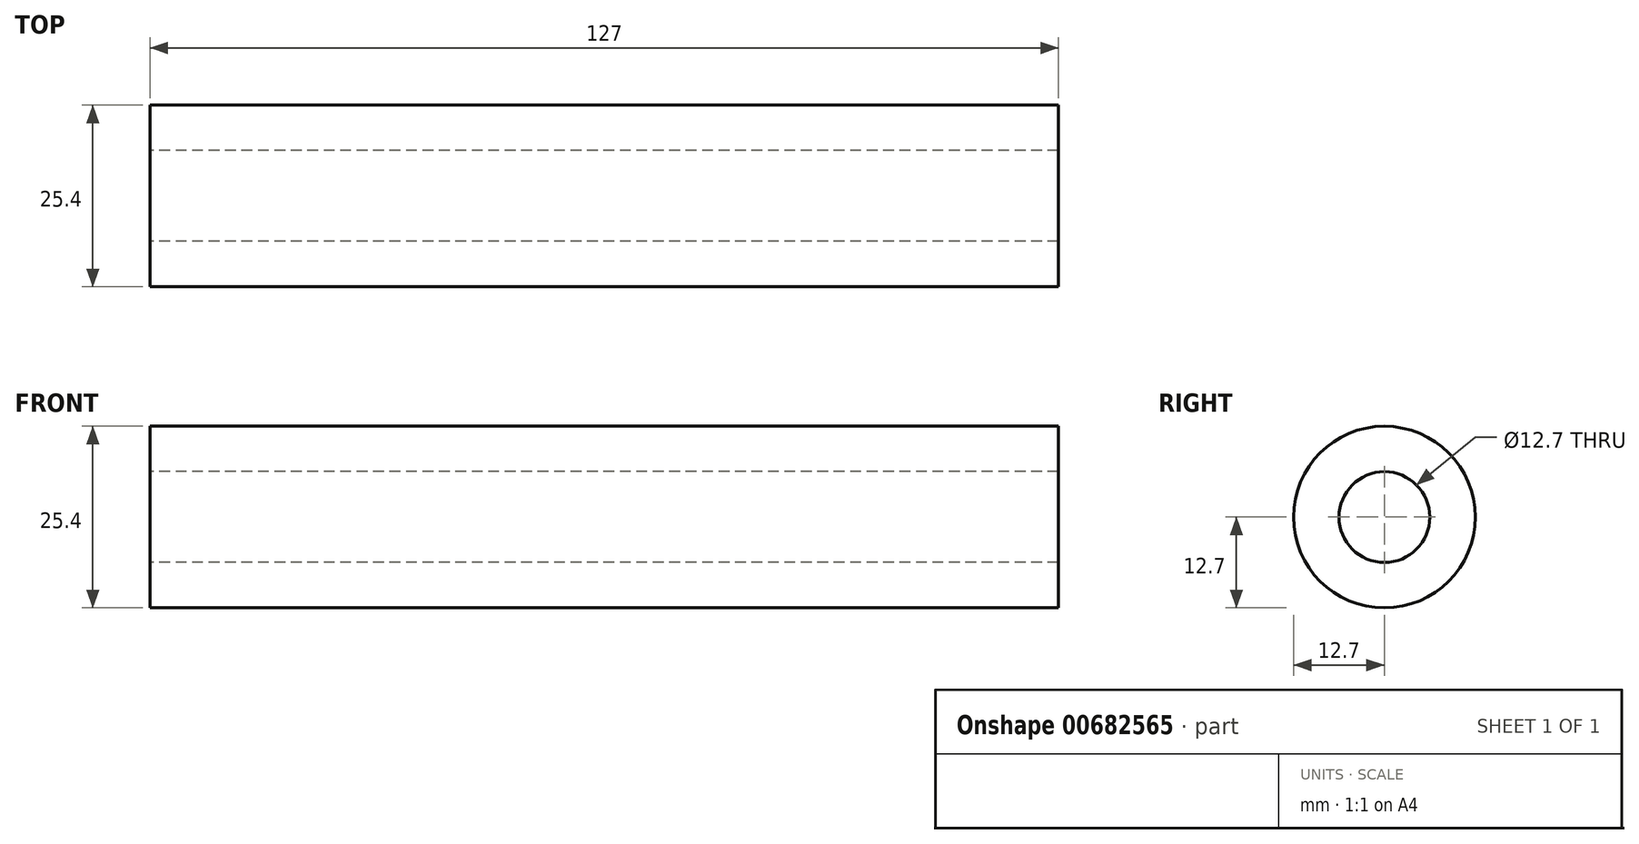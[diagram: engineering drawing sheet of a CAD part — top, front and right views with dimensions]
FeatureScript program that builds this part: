
annotation { "Feature Type Name" : "Feature", "Feature Type Description" : "" }
export const myFeature = defineFeature(function(context is Context, id is Id, definition is map)
    precondition{}
    {
        {
            var Q0;
            Q0=qCreatedBy(makeId("Right.planeOp"),FACE);
            var sketch = newSketch(context, id + "F0", { "sketchPlane" : qUnion([Q0])});
            skCircle(sketch, "E0", {"center": v(0, 0) * mm, "radius": 12.7 * mm});
            skCircle(sketch, "E1", {"center": v(0, 0) * mm, "radius": 6.35 * mm});
            skSolve(sketch);
        }
        {
            var Q0;
            Q0 = qSketchRegion(id + "F0", true);
            extrude(context, id + "F1", {"entities" : qUnion([Q0]), "depth" : 127 * mm, "offsetDistance" : 25.4 * mm});
        }
    });
